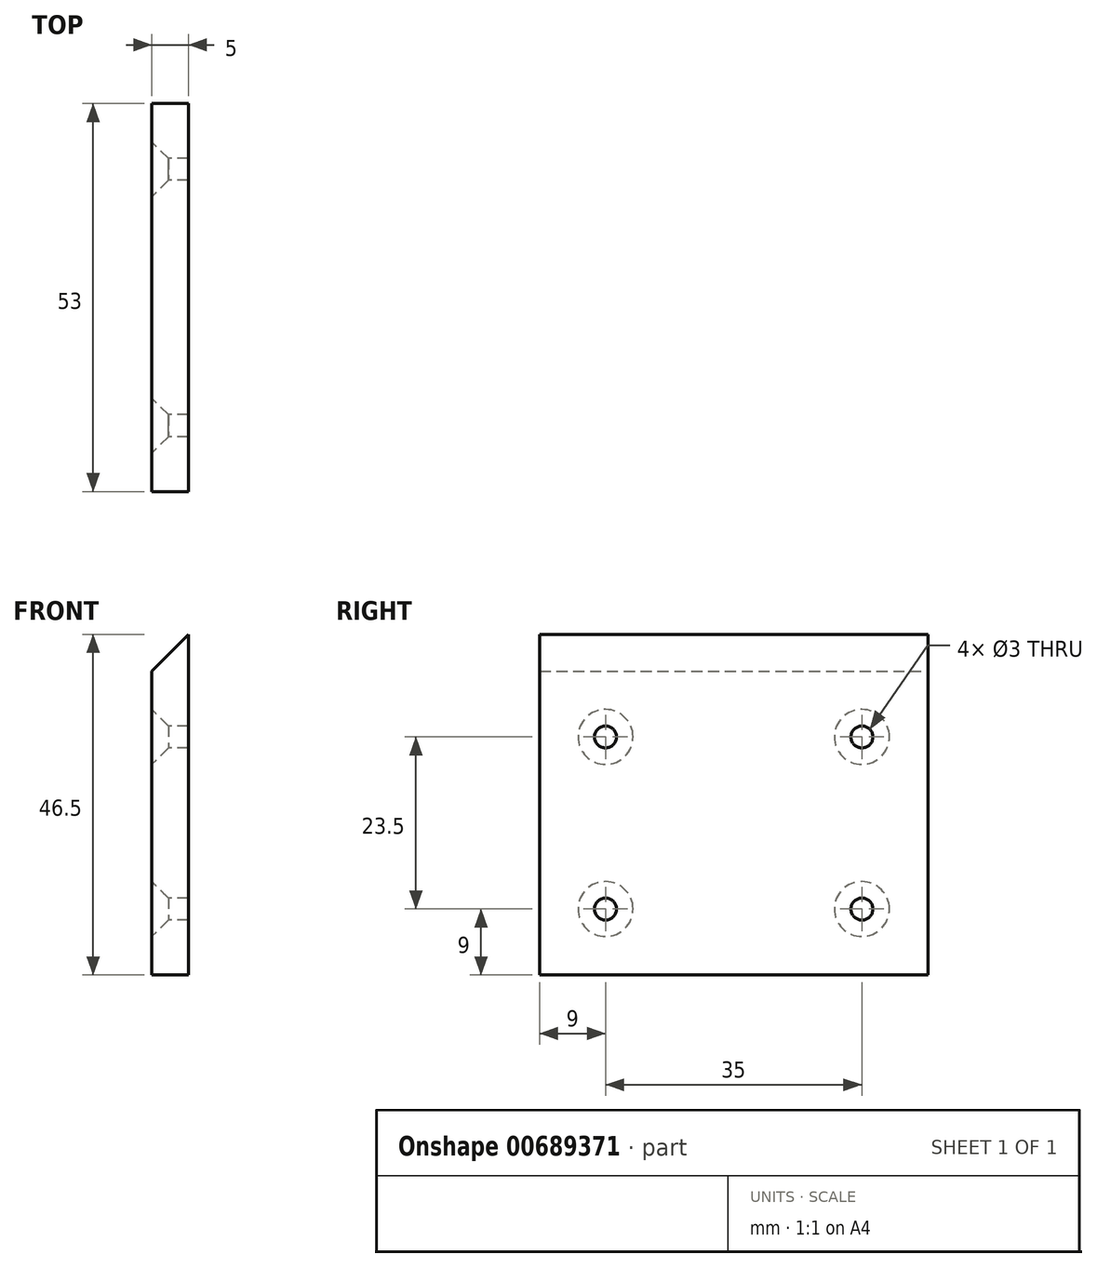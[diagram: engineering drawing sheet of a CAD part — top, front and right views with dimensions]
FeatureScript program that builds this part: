
annotation { "Feature Type Name" : "Feature", "Feature Type Description" : "" }
export const myFeature = defineFeature(function(context is Context, id is Id, definition is map)
    precondition{}
    {
        {
            var Q0;
            Q0=qCreatedBy(makeId("Front.planeOp"),FACE);
            var sketch = newSketch(context, id + "F0", { "sketchPlane" : qUnion([Q0])});
            skLineSegment(sketch, "E0.bottom", {"start": v(0, 0) * mm, "end": v(5, 0) * mm});
            skLineSegment(sketch, "E0.left", {"start": v(0, 0) * mm, "end": v(0, 41.5) * mm});
            skLineSegment(sketch, "E0.right", {"start": v(5, 0) * mm, "end": v(5, 46.5) * mm});
            skLineSegment(sketch, "E1", {"start": v(5, 46.5) * mm, "end": v(0, 41.5) * mm});
            skSolve(sketch);
        }
        {
            var Q0;
            Q0=qSketchRegion(id+"F0",true);
            extrude(context, id + "F1", {"entities" : qUnion([Q0]), "depth" : 53 * mm});
        }
        {
            var Q0;
            Q0=makeQuery(id+"F1.opExtrude","SWEPT_FACE",FACE,{"disambiguationData":[OSD([sQuery(id+"F0.wireOp",EDGE,"E0.left")])]});
            var sketch = newSketch(context, id + "F2", { "sketchPlane" : qUnion([Q0])});
            skPoint(sketch, "E2", {"position": v(9, 32.5) * mm});
            skPoint(sketch, "E3", {"position": v(44, 32.5) * mm});
            skPoint(sketch, "E4", {"position": v(44, 9) * mm});
            skPoint(sketch, "E5", {"position": v(9, 9) * mm});
            skSolve(sketch);
        }
        {
            var Q0;
            Q0=sQuery(id+"F2.wireOp",VERTEX,"E2");
            var Q1;
            Q1=sQuery(id+"F2.wireOp",VERTEX,"E3");
            var Q2;
            Q2=sQuery(id+"F2.wireOp",VERTEX,"E4");
            var Q3;
            Q3=sQuery(id+"F2.wireOp",VERTEX,"E5");
            var Q4;
            Q4=makeQuery(id+"F1.opExtrude","SWEPT_BODY",BODY,{"disambiguationData":[OSD([sQuery(id+"F0.wireOp",EDGE,"E0.bottom"),sQuery(id+"F0.wireOp",EDGE,"E0.left"),sQuery(id+"F0.wireOp",EDGE,"E0.right"),sQuery(id+"F0.wireOp",EDGE,"E1")])]});
            hole(context, id + "F3", {"style" : HoleStyle.C_SINK, "endStyle" : HoleEndStyle.THROUGH, "holeDiameter" : 3 * mm, "cSinkDiameter" : 7.5 * mm, "cSinkAngle" : 90 * degree, "majorDiameter" : 5 * mm, "isTappedThrough" : true, "tappedDepth" : 12 * mm, "tapClearance" : 3, "startFromSketch" : true, "locations" : qUnion([Q0, Q1, Q2, Q3]), "scope" : qUnion([Q4])});
        }
    });
